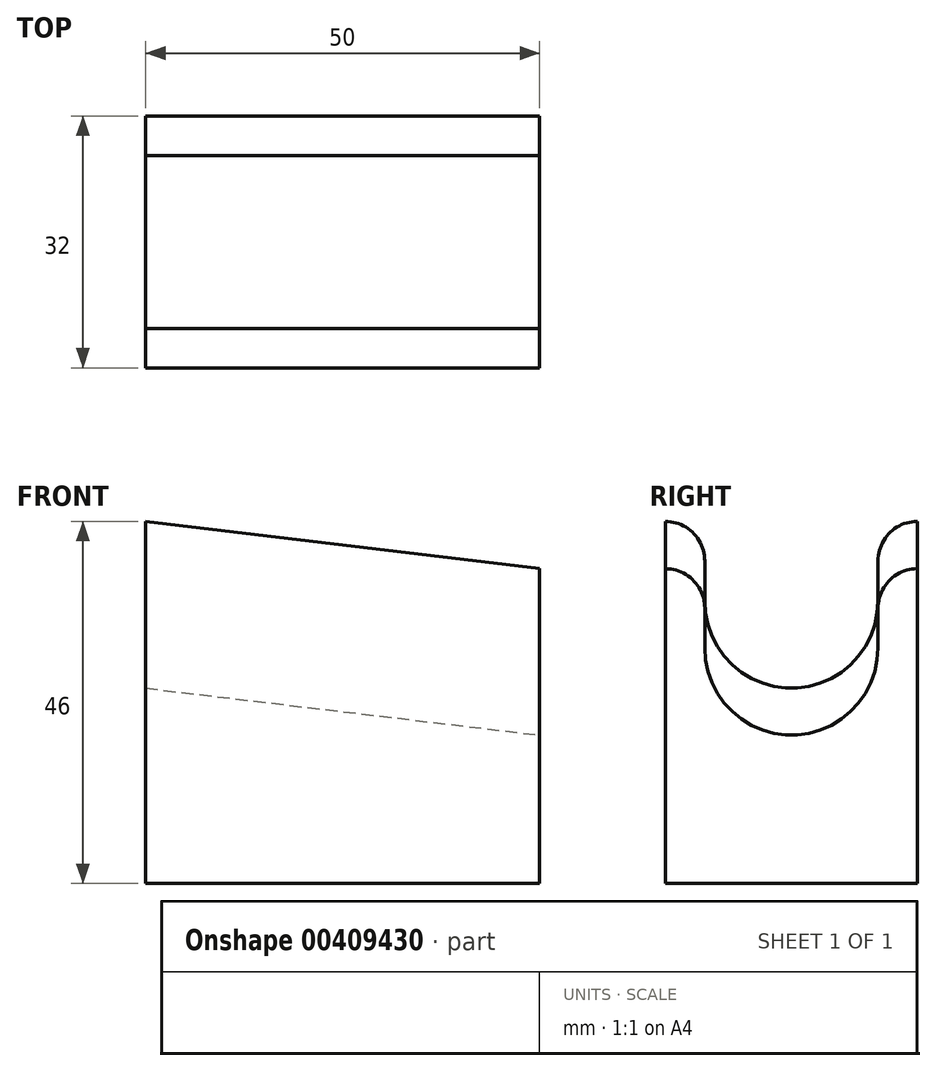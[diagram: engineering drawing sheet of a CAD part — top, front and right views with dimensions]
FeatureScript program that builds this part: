
annotation { "Feature Type Name" : "Feature", "Feature Type Description" : "" }
export const myFeature = defineFeature(function(context is Context, id is Id, definition is map)
    precondition{}
    {
        {
            var Q0;
            Q0=qCreatedBy(makeId("Front.planeOp"),FACE);
            var sketch = newSketch(context, id + "F0", { "sketchPlane" : qUnion([Q0])});
            skLineSegment(sketch, "E0", {"start": v(0, 0) * mm, "end": v(0, 46) * mm});
            skLineSegment(sketch, "E1", {"start": v(0, 0) * mm, "end": v(50, 0) * mm});
            skLineSegment(sketch, "E2", {"start": v(50, 0) * mm, "end": v(50, 40) * mm});
            skLineSegment(sketch, "E3", {"start": v(50, 40) * mm, "end": v(0, 46) * mm});
            skSolve(sketch);
        }
        {
            var Q0;
            Q0 = qSketchRegion(id + "F0", true);
            extrude(context, id + "F1", {"entities" : qUnion([Q0]), "oppositeDirection" : true, "depth" : 32 * mm, "offsetDistance" : 25 * mm});
        }
        {
            var Q0;
            Q0=makeQuery(id+"F1.opExtrude","SWEPT_EDGE",EDGE,{"disambiguationData":[OSD([sQuery(id+"F0.wireOp",EDGE,"E2"),sQuery(id+"F0.wireOp",EDGE,"E3")])]});
            cPlane(context, id + "F2", {"entities" : qUnion([Q0]), "cplaneType" : CPlaneType.LINE_ANGLE, "offset" : 25 * mm, "angle" : 83.2 * degree, "width" : 150 * mm, "height" : 150 * mm});
        }
        {
            var Q0;
            Q0=qCreatedBy(id+"F2.planeOp",FACE);
            var sketch = newSketch(context, id + "F3", { "sketchPlane" : qUnion([Q0])});
            skArc(sketch, "E4", {"start": v(5, 35.64) * mm, "mid": v(16, 24.64) * mm, "end": v(27, 35.64) * mm});
            skLineSegment(sketch, "E5", {"start": v(5, 47.63) * mm, "end": v(5, 35.64) * mm});
            skLineSegment(sketch, "E6", {"start": v(27, 47.63) * mm, "end": v(27, 35.64) * mm});
            skLineSegment(sketch, "E7", {"start": v(5, 47.63) * mm, "end": v(27, 47.63) * mm});
            skSolve(sketch);
        }
        {
            var Q0;
            Q0 = qSketchRegion(id + "F3", true);
            extrude(context, id + "F4", {"entities" : qUnion([Q0]), "operationType" : NewBodyOperationType.REMOVE, "oppositeDirection" : true, "depth" : 110 * mm, "offsetDistance" : 25 * mm, "symmetric" : true});
        }
        {
            var Q0;
            Q0=makeQuery(id+"F4.boolean.opBoolean","INTERSECT",EDGE,{"derivedFrom":[makeQuery(id+"F1.opExtrude","SWEPT_FACE",FACE,{"disambiguationData":[OSD([sQuery(id+"F0.wireOp",EDGE,"E3")])]}),makeQuery(id+"F4.opExtrude","SWEPT_FACE",FACE,{"disambiguationData":[OSD([sQuery(id+"F3.wireOp",EDGE,"E6")])]})]});
            var Q1;
            Q1=makeQuery(id+"F4.boolean.opBoolean","INTERSECT",EDGE,{"derivedFrom":[makeQuery(id+"F1.opExtrude","SWEPT_FACE",FACE,{"disambiguationData":[OSD([sQuery(id+"F0.wireOp",EDGE,"E3")])]}),makeQuery(id+"F4.opExtrude","SWEPT_FACE",FACE,{"disambiguationData":[OSD([sQuery(id+"F3.wireOp",EDGE,"E5")])]})]});
            fillet(context, id + "F5", {"entities" : qUnion([Q0, Q1]), "tangentPropagation" : true, "radius" : 5 * mm, "defaultsChanged" : false, "vertexSettings" : [], "allowEdgeOverflow" : false});
        }
    });
